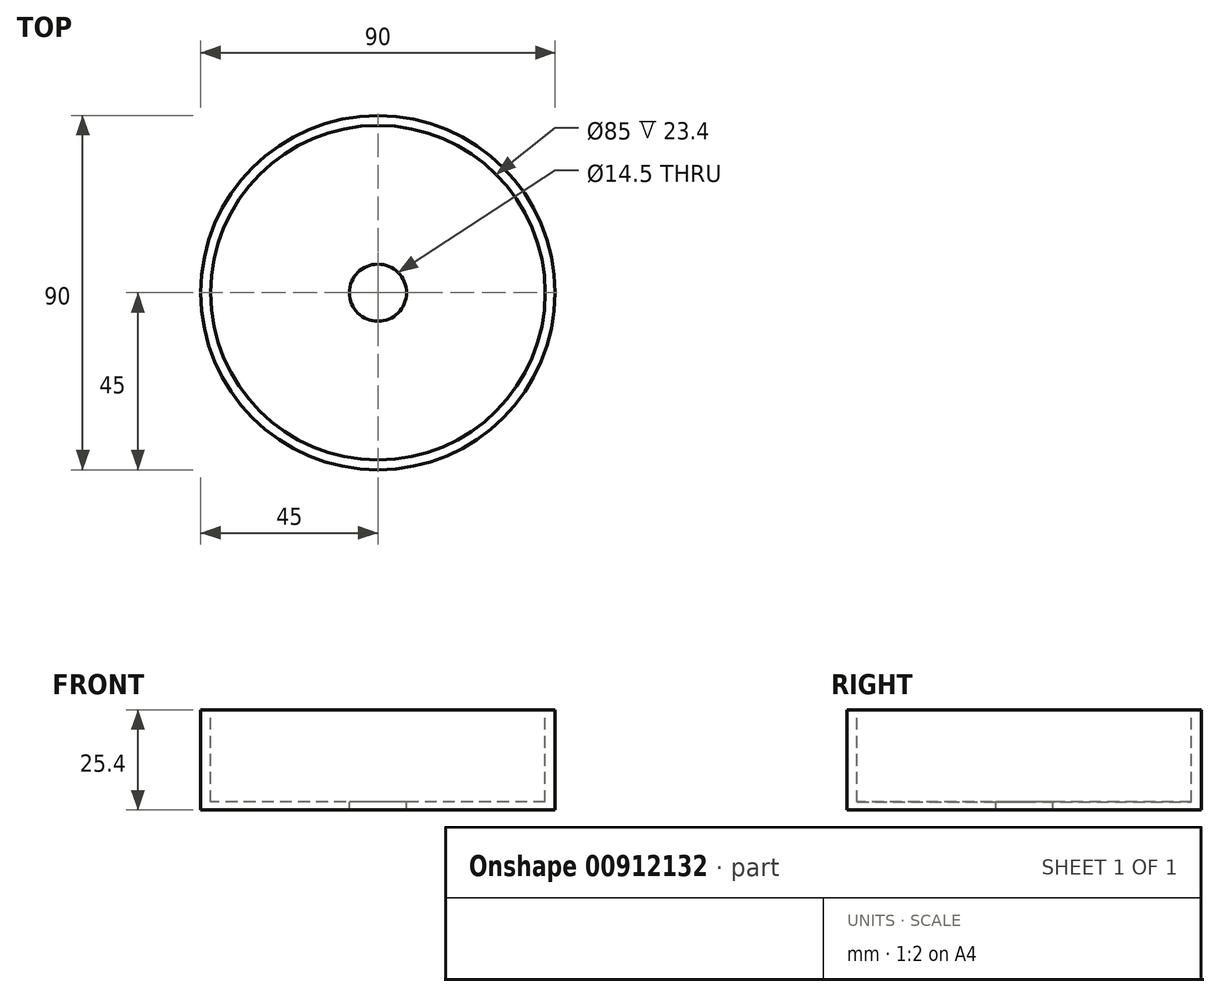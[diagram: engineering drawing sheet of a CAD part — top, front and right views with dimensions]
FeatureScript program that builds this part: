
annotation { "Feature Type Name" : "Feature", "Feature Type Description" : "" }
export const myFeature = defineFeature(function(context is Context, id is Id, definition is map)
    precondition{}
    {
        {
            var Q0;
            Q0=qCreatedBy(makeId("Top.planeOp"),FACE);
            var sketch = newSketch(context, id + "F0", { "sketchPlane" : qUnion([Q0])});
            skCircle(sketch, "E0", {"center": v(0, 0) * mm, "radius": 45 * mm});
            skSolve(sketch);
        }
        {
            var Q0;
            Q0 = qSketchRegion(id + "F0", true);
            extrude(context, id + "F1", {"entities" : qUnion([Q0]), "depth" : 25.4 * mm, "offsetDistance" : 25 * mm});
        }
        {
            var Q0;
            Q0=makeQuery(id+"F1.opExtrude","CAP_FACE",FACE,{"disambiguationData":[OSD([sQuery(id+"F0.wireOp",EDGE,"E0")])],"isStart":false});
            var sketch = newSketch(context, id + "F2", { "sketchPlane" : qUnion([Q0])});
            skCircle(sketch, "E1", {"center": v(0, 0) * mm, "radius": 42.5 * mm});
            skSolve(sketch);
        }
        {
            var Q0;
            Q0=makeQuery(id+"F2.imprint","IMPRINT",FACE,{"disambiguationData":[TD([[makeQuery(id+"F2.imprint","IMPRINT",EDGE,{"derivedFrom":sQuery(id+"F2.wireOp",EDGE,"E1")}),1.0]])]});
            var Q1;
            Q1=makeQuery(id+"F1.opExtrude","CAP_FACE",FACE,{"disambiguationData":[OSD([sQuery(id+"F0.wireOp",EDGE,"E0")])],"isStart":true});
            extrude(context, id + "F3", {"entities" : qUnion([Q0]), "operationType" : NewBodyOperationType.REMOVE, "endBound" : BoundingType.UP_TO_SURFACE, "oppositeDirection" : true, "depth" : 10 * mm, "endBoundEntityFace" : qUnion([Q1]), "hasOffset" : true, "offsetDistance" : 2 * mm});
        }
        {
            var Q0;
            Q0=makeQuery(id+"F3.boolean.opBoolean","COPY",FACE,{"derivedFrom":makeQuery(id+"F3.opExtrude","CAP_FACE",FACE,{"disambiguationData":[OSD([sQuery(id+"F2.wireOp",EDGE,"E1")])],"isStart":false})});
            var Q1;
            Q1=makeQuery(id+"F3.boolean.opBoolean","COPY",FACE,{"derivedFrom":makeQuery(id+"F3.opExtrude","CAP_FACE",FACE,{"disambiguationData":[OSD([sQuery(id+"F2.wireOp",EDGE,"E1")])],"isStart":false})});
            var sketch = newSketch(context, id + "F4", { "sketchPlane" : qUnion([Q0, Q1])});
            skCircle(sketch, "E2", {"center": v(0, 0) * mm, "radius": 7.25 * mm});
            skSolve(sketch);
        }
        {
            var Q0;
            Q0=makeQuery(id+"F4.imprint","IMPRINT",FACE,{"disambiguationData":[TD([[makeQuery(id+"F4.imprint","IMPRINT",EDGE,{"derivedFrom":sQuery(id+"F4.wireOp",EDGE,"E2")}),1.0]])]});
            extrude(context, id + "F5", {"entities" : qUnion([Q0]), "operationType" : NewBodyOperationType.REMOVE, "oppositeDirection" : true, "depth" : 25 * mm, "offsetDistance" : 25 * mm});
        }
    });
